FCSTD DOCUMENT  (FreeCAD 0.19R24291 (Git))
Label: v1-180-assembly
License: Other
LicenseURL: GPL3
objects: App::Link×50, App::Part×6, App::DocumentObjectGroup×2, PartDesign::CoordinateSystem×1, App::FeaturePython×1
note: 1 computed B-rep shape members (.brp) not serialized (recipe doc carries the construction recipe, not evaluated geometry)
EXTERNAL_REF file=../WIP/component-assembly/frame-assembly.FCStd obj=LCS_main_frame
EXTERNAL_REF file=../WIP/component-assembly/frame-assembly.FCStd obj=Part054
EXTERNAL_REF file=../WIP/component-assembly/foot-assembly.FCStd obj=LCS_foot
EXTERNAL_REF file=../WIP/component-assembly/foot-assembly.FCStd obj=Part
EXTERNAL_REF file=../WIP/component-assembly/ab-x-motor-assembly.FCStd obj=LCS_ab_x_motor
EXTERNAL_REF file=../WIP/component-assembly/ab-x-motor-assembly.FCStd obj=Part
EXTERNAL_REF file=../WIP/component-assembly/ab-y-motor-assembly.FCStd obj=LCS_ab_y_motor
EXTERNAL_REF file=../WIP/component-assembly/ab-y-motor-assembly.FCStd obj=Part
EXTERNAL_REF file=../WIP/component-assembly/linear-rail-assembly.FCStd obj=LCS_0001
EXTERNAL_REF file=../WIP/component-assembly/linear-rail-assembly.FCStd obj=y_rails
EXTERNAL_REF file=../WIP/component-assembly/linear-rail-assembly.FCStd obj=LCS_0002
EXTERNAL_REF file=../WIP/component-assembly/linear-rail-assembly.FCStd obj=z_rails
EXTERNAL_REF file=../WIP/component-assembly/y-carrier-left-1515-assembly.FCStd obj=LCS_Y_carrier_left
EXTERNAL_REF file=../WIP/component-assembly/y-carrier-left-1515-assembly.FCStd obj=Part
EXTERNAL_REF file=../WIP/component-assembly/y-carrier-right-1515-assembly.FCStd obj=LCS_Y_carrier_right
EXTERNAL_REF file=../WIP/component-assembly/y-carrier-right-1515-assembly.FCStd obj=Part
EXTERNAL_REF file=../WIP/component-assembly/linear-rail-assembly.FCStd obj=LCS_0
EXTERNAL_REF file=../WIP/component-assembly/linear-rail-assembly.FCStd obj=x_rail
EXTERNAL_REF file=../WIP/component-assembly/z-motor-left-assembly.FCStd obj=LCS_z_motor_left
EXTERNAL_REF file=../WIP/component-assembly/z-motor-left-assembly.FCStd obj=Part
EXTERNAL_REF file=../WIP/component-assembly/z-motor-right-assembly.FCStd obj=LCS_z_motor_right
EXTERNAL_REF file=../WIP/component-assembly/z-motor-right-assembly.FCStd obj=Part
EXTERNAL_REF file=../WIP/component-assembly/bed-assembly.FCStd obj=LCS_0
EXTERNAL_REF file=../WIP/component-assembly/bed-assembly.FCStd obj=bed_assembly
EXTERNAL_REF file=../WIP/component-assembly/z-belt-assembly.FCStd obj=LCS_z_belt
EXTERNAL_REF file=../WIP/component-assembly/z-belt-assembly.FCStd obj=Part
EXTERNAL_REF file=../WIP/component-assembly/xy-belt-assembly.FCStd obj=LCS_xy_belt
EXTERNAL_REF file=../WIP/component-assembly/xy-belt-assembly.FCStd obj=Part
EXTERNAL_REF file=../WIP/component-assembly/bottom-panel-assembly.FCStd obj=LCS_bottom_panel_assembly
EXTERNAL_REF file=../WIP/component-assembly/bottom-panel-assembly.FCStd obj=Part007
EXTERNAL_REF file=../WIP/component-assembly/extruder-cable-end-assembly.FCStd obj=LCS_extruder_cable_mounter
EXTERNAL_REF file=../WIP/component-assembly/extruder-cable-end-assembly.FCStd obj=Part198
EXTERNAL_REF file=../WIP/component-assembly/y-endstop-assembly.FCStd obj=LCS_y_endstop
EXTERNAL_REF file=../WIP/component-assembly/y-endstop-assembly.FCStd obj=Part
EXTERNAL_REF file=../WIP/component-assembly/x-endstop-flag-assembly.FCStd obj=LCS_x_endstop_flag
EXTERNAL_REF file=../WIP/component-assembly/x-endstop-flag-assembly.FCStd obj=Part001
EXTERNAL_REF file=../WIP/component-assembly/sherpa-mini-assembly.FCStd obj=LCS_sherpa_mini
EXTERNAL_REF file=../WIP/component-assembly/sherpa-mini-assembly.FCStd obj=Part
EXTERNAL_REF file=../WIP/component-assembly/z-block-mount-left-assembly.FCStd obj=LCS_z_rail_block_mount_y_slider_1
EXTERNAL_REF file=../WIP/component-assembly/z-block-mount-left-assembly.FCStd obj=Part
EXTERNAL_REF file=../WIP/component-assembly/z-idler-left-assembly.FCStd obj=LCS_Z_idler_left
EXTERNAL_REF file=../WIP/component-assembly/z-idler-left-assembly.FCStd obj=Part
EXTERNAL_REF file=../WIP/component-assembly/z-idler-right-assembly.FCStd obj=LCS_Z_idler_right
EXTERNAL_REF file=../WIP/component-assembly/z-idler-right-assembly.FCStd obj=Part001
EXTERNAL_REF file=../WIP/component-assembly/addon-filament-guide-arm-assembly.FCStd obj=LCS_filament_guide
EXTERNAL_REF file=../WIP/component-assembly/addon-filament-guide-arm-assembly.FCStd obj=Part002
EXTERNAL_REF file=../WIP/component-assembly/front-left-idler-assembly.FCStd obj=LCS_left_idler
EXTERNAL_REF file=../WIP/component-assembly/front-left-idler-assembly.FCStd obj=Part
EXTERNAL_REF file=../WIP/component-assembly/front-right-idler-assembly.FCStd obj=LCS_right_idler
EXTERNAL_REF file=../WIP/component-assembly/front-right-idler-assembly.FCStd obj=Part001
EXTERNAL_REF file=../WIP/component-assembly/addon-camera-assembly.FCStd obj=LCS_camera
EXTERNAL_REF file=../WIP/component-assembly/addon-camera-assembly.FCStd obj=Part001
EXTERNAL_REF file=../WIP/component-assembly/spool-holder-assembly.FCStd obj=LCS_spool_holder
EXTERNAL_REF file=../WIP/component-assembly/spool-holder-assembly.FCStd obj=Part196
EXTERNAL_REF file=../WIP/component-assembly/LCD-assembly.FCStd obj=LCS_LCD
EXTERNAL_REF file=../WIP/component-assembly/LCD-assembly.FCStd obj=Part
EXTERNAL_REF file=../WIP/component-assembly/left-panel-assembly.FCStd obj=LCS_left_panel
EXTERNAL_REF file=../WIP/component-assembly/left-panel-assembly.FCStd obj=Part025
EXTERNAL_REF file=../WIP/component-assembly/top-panel-assembly.FCStd obj=LCS_top_panel
EXTERNAL_REF file=../WIP/component-assembly/top-panel-assembly.FCStd obj=Part042
EXTERNAL_REF file=../WIP/component-assembly/rear-bottom-panel-assembly.FCStd obj=LCS_back_bottom_panel
EXTERNAL_REF file=../WIP/component-assembly/rear-bottom-panel-assembly.FCStd obj=Part003
EXTERNAL_REF file=../WIP/component-assembly/rear-top-panel-assembly.FCStd obj=LCS_back_top_panel
EXTERNAL_REF file=../WIP/component-assembly/rear-top-panel-assembly.FCStd obj=Part004
EXTERNAL_REF file=../WIP/component-assembly/front-panel-assembly.FCStd obj=LCS_front_panel
EXTERNAL_REF file=../WIP/component-assembly/front-panel-assembly.FCStd obj=Part046
EXTERNAL_REF file=../WIP/component-assembly/neo-pixel-assembly.FCStd obj=LCS_neopizel
EXTERNAL_REF file=../WIP/component-assembly/neo-pixel-assembly.FCStd obj=Part
EXTERNAL_REF file=../WIP/component-assembly/cherrymz-button-assembly.FCStd obj=LCS_cherrymx_button
EXTERNAL_REF file=../WIP/component-assembly/cherrymz-button-assembly.FCStd obj=Part
EXTERNAL_REF file=../WIP/component-assembly/air-filter-assembly.FCStd obj=LCS_air_filter
EXTERNAL_REF file=../WIP/component-assembly/air-filter-assembly.FCStd obj=Part
EXTERNAL_REF file=../WIP/component-assembly/add-on-ptfe-tube-guide-assembly.FCStd obj=LCS_ptfe_tube_guide
EXTERNAL_REF file=../WIP/component-assembly/add-on-ptfe-tube-guide-assembly.FCStd obj=Part
EXTERNAL_REF file=../WIP/component-assembly/counter-weight-spring-box-assembly.FCStd obj=LCS_counter_spring_box
EXTERNAL_REF file=../WIP/component-assembly/counter-weight-spring-box-assembly.FCStd obj=Part
EXTERNAL_REF file=../WIP/component-assembly/counter-weight-spring-box-assembly.FCStd obj=LCS_counter_weight_top_arm
EXTERNAL_REF file=../WIP/component-assembly/counter-weight-spring-box-assembly.FCStd obj=Part001
EXTERNAL_REF file=../WIP/component-assembly/z-block-mount-right-counter-weight-assembly.FCStd obj=LCS_z_rail_block_mount_x_slider
EXTERNAL_REF file=../WIP/component-assembly/z-block-mount-right-counter-weight-assembly.FCStd obj=Part001
EXTERNAL_REF file=../WIP/component-assembly/toolhead-sherpa-pcb-1515-assembly.FCStd obj=LCS_toolhead_1515
EXTERNAL_REF file=../WIP/component-assembly/toolhead-sherpa-pcb-1515-assembly.FCStd obj=Part197
EXTERNAL_REF file=../WIP/component-assembly/right-panel-assembly.FCStd obj=LCS_right_panel
EXTERNAL_REF file=../WIP/component-assembly/right-panel-assembly.FCStd obj=Part005
EXTERNAL_REF file=../WIP/component-assembly/side-blower-4028-assembly.FCStd obj=LCS_aux_fan
EXTERNAL_REF file=../WIP/component-assembly/side-blower-4028-assembly.FCStd obj=Part

FEATURE [App::DocumentObjectGroup] Parts
FEATURE [PartDesign::CoordinateSystem] LCS_Origin
  AttacherType = Attacher::AttachEngine3D
  MapMode = 2
  Support = -> [X_Axis]
FEATURE [App::DocumentObjectGroup] Constraints
FEATURE [App::FeaturePython] Variables  # WARN: FeaturePython — macro-defined, semantics opaque (R4)
FEATURE [App::Link] frame_assembly_main_frame  label="frame"
  AssemblyType = Asm4EE
  AttachedBy = #LCS_main_frame
  AttachedTo = Parent Assembly#LCS_Origin
  ElementCount = 0
  LinkTransform = false
  Scale = 1
  ScaleVector = (1,1,1)
  ShowElement = true
  expr: Placement = LCS_Origin.Placement * AttachmentOffset * frame_assembly#LCS_main_frame.Placement ^ -1
FEATURE [App::Link] Unnamed2_foot  label="foot-1"
  AssemblyType = Asm4EE
  AttachedBy = #LCS_foot
  AttachedTo = Parent Assembly#LCS_Origin
  AttachmentOffset = pos=(-170,15,-30) rot=(0,0,1;3.14159rad)
  ElementCount = 0
  LinkPlacement = pos=(-170,15,-30) rot=(0,0,1;3.14159rad)
  LinkTransform = false
  Placement = pos=(-170,15,-30) rot=(0,0,1;3.14159rad)
  Scale = 1
  ScaleVector = (1,1,1)
  ShowElement = true
  expr: Placement = LCS_Origin.Placement * AttachmentOffset * foot_assembly#LCS_foot.Placement ^ -1
FEATURE [App::Link] Unnamed2_foot001  label="foot-2"
  AssemblyType = Asm4EE
  AttachedBy = #LCS_foot
  AttachedTo = Parent Assembly#LCS_Origin
  AttachmentOffset = pos=(170,15,-30) rot=(0,0,1;4.71239rad)
  ElementCount = 0
  LinkPlacement = pos=(170,15,-30) rot=(0,0,1;4.71239rad)
  LinkTransform = false
  Placement = pos=(170,15,-30) rot=(0,0,1;4.71239rad)
  Scale = 1
  ScaleVector = (1,1,1)
  ShowElement = true
  expr: Placement = LCS_Origin.Placement * AttachmentOffset * foot_assembly#LCS_foot.Placement ^ -1
FEATURE [App::Link] Unnamed2_foot002  label="foot-3"
  AssemblyType = Asm4EE
  AttachedBy = #LCS_foot
  AttachedTo = Parent Assembly#LCS_Origin
  AttachmentOffset = pos=(170,355,-30) rot=(0,0,1;0rad)
  ElementCount = 0
  LinkPlacement = pos=(170,355,-30) rot=(0,0,1;0rad)
  LinkTransform = false
  Placement = pos=(170,355,-30) rot=(0,0,1;0rad)
  Scale = 1
  ScaleVector = (1,1,1)
  ShowElement = true
  expr: Placement = LCS_Origin.Placement * AttachmentOffset * foot_assembly#LCS_foot.Placement ^ -1
FEATURE [App::Link] Unnamed2_foot003  label="foot-4"
  AssemblyType = Asm4EE
  AttachedBy = #LCS_foot
  AttachedTo = Parent Assembly#LCS_Origin
  AttachmentOffset = pos=(-170,355,-30) rot=(0,0,1;1.5708rad)
  ElementCount = 0
  LinkPlacement = pos=(-170,355,-30) rot=(0,0,1;1.5708rad)
  LinkTransform = false
  Placement = pos=(-170,355,-30) rot=(0,0,1;1.5708rad)
  Scale = 1
  ScaleVector = (1,1,1)
  ShowElement = true
  expr: Placement = LCS_Origin.Placement * AttachmentOffset * foot_assembly#LCS_foot.Placement ^ -1
FEATURE [App::Link] left_motor_assembly_ab_x_motor  label="ab-x-motor"
  AssemblyType = Asm4EE
  AttachedBy = #LCS_ab_x_motor
  AttachedTo = Parent Assembly#LCS_Origin
  AttachmentOffset = pos=(-155,370,310) rot=(0,0,1;0rad)
  ElementCount = 0
  LinkPlacement = pos=(-155,370,310) rot=(0,0,1;0rad)
  LinkTransform = false
  Placement = pos=(-155,370,310) rot=(0,0,1;0rad)
  Scale = 1
  ScaleVector = (1,1,1)
  ShowElement = true
  expr: Placement = LCS_Origin.Placement * AttachmentOffset * ab_x_motor_assembly#LCS_ab_x_motor.Placement ^ -1
FEATURE [App::Link] right_motor_assembly_ab_y_motor  label="ab-y-motor"
  AssemblyType = Asm4EE
  AttachedBy = #LCS_ab_y_motor
  AttachedTo = Parent Assembly#LCS_Origin
  AttachmentOffset = pos=(155,370,310) rot=(0,0,1;0rad)
  ElementCount = 0
  LinkPlacement = pos=(155,370,310) rot=(0,0,1;0rad)
  LinkTransform = false
  Placement = pos=(155,370,310) rot=(0,0,1;0rad)
  Scale = 1
  ScaleVector = (1,1,1)
  ShowElement = true
  expr: Placement = LCS_Origin.Placement * AttachmentOffset * ab_y_motor_assembly#LCS_ab_y_motor.Placement ^ -1
FEATURE [App::Link] linear_rail_assembly_y_rails  label="y_rails"
  AssemblyType = Asm4EE
  AttachedBy = #LCS_0001
  AttachedTo = Parent Assembly#LCS_Origin
  ElementCount = 0
  LinkTransform = false
  Scale = 1
  ScaleVector = (1,1,1)
  ShowElement = true
  expr: Placement = LCS_Origin.Placement * AttachmentOffset * linear_rail_assembly#LCS_0001.Placement ^ -1
FEATURE [App::Link] linear_rail_assembly_z_rails  label="z_rails"
  AssemblyType = Asm4EE
  AttachedBy = #LCS_0002
  AttachedTo = Parent Assembly#LCS_Origin
  ElementCount = 0
  LinkTransform = false
  Scale = 1
  ScaleVector = (1,1,1)
  ShowElement = true
  expr: Placement = LCS_Origin.Placement * AttachmentOffset * linear_rail_assembly#LCS_0002.Placement ^ -1
FEATURE [App::Link] Y_carrier_left  label="Y-carrier-left"
  AssemblyType = Asm4EE
  AttachedBy = #LCS_Y_carrier_left
  AttachedTo = Parent Assembly#LCS_Origin
  AttachmentOffset = pos=(-156,203,310) rot=(0,0,1;0rad)
  ElementCount = 0
  LinkPlacement = pos=(-156,203,310) rot=(0,0,1;0rad)
  LinkTransform = false
  Placement = pos=(-156,203,310) rot=(0,0,1;0rad)
  Scale = 1
  ScaleVector = (1,1,1)
  ShowElement = true
  expr: Placement = LCS_Origin.Placement * AttachmentOffset * y_carrier_left_1515_assembly#LCS_Y_carrier_left.Placement ^ -1
FEATURE [App::Link] Y_carrier_right  label="Y-carrier-right"
  AssemblyType = Asm4EE
  AttachedBy = #LCS_Y_carrier_right
  AttachedTo = Parent Assembly#LCS_Origin
  AttachmentOffset = pos=(155,203,310) rot=(0,0,1;0rad)
  ElementCount = 0
  LinkPlacement = pos=(155,203,310) rot=(0,0,1;0rad)
  LinkTransform = false
  Placement = pos=(155,203,310) rot=(0,0,1;0rad)
  Scale = 1
  ScaleVector = (1,1,1)
  ShowElement = true
  expr: Placement = LCS_Origin.Placement * AttachmentOffset * y_carrier_right_1515_assembly#LCS_Y_carrier_right.Placement ^ -1
FEATURE [App::Link] linear_rail_assembly_x_rail  label="x_rail"
  AssemblyType = Asm4EE
  AttachedBy = #LCS_0
  AttachedTo = Parent Assembly#LCS_Origin
  AttachmentOffset = pos=(0,0,-2.5) rot=(0,0,1;0rad)
  ElementCount = 0
  LinkPlacement = pos=(0,0,-2.5) rot=(0,0,1;0rad)
  LinkTransform = false
  Placement = pos=(0,0,-2.5) rot=(0,0,1;0rad)
  Scale = 1
  ScaleVector = (1,1,1)
  ShowElement = true
  expr: Placement = LCS_Origin.Placement * AttachmentOffset * linear_rail_assembly#LCS_0.Placement ^ -1
FEATURE [App::Link] z_motor_left_assembly_z_motor_left  label="z-motor-left-front"
  AssemblyType = Asm4EE
  AttachedBy = #LCS_z_motor_left
  AttachedTo = Parent Assembly#LCS_Origin
  AttachmentOffset = pos=(-155,117,0) rot=(0,0,1;0rad)
  ElementCount = 0
  LinkPlacement = pos=(-155,117,0) rot=(0,0,1;0rad)
  LinkTransform = false
  Placement = pos=(-155,117,0) rot=(0,0,1;0rad)
  Scale = 1
  ScaleVector = (1,1,1)
  ShowElement = true
  expr: Placement = LCS_Origin.Placement * AttachmentOffset * z_motor_left_assembly#LCS_z_motor_left.Placement ^ -1
FEATURE [App::Link] z_motor_left_back  label="z-motor-left-back"
  AssemblyType = Asm4EE
  AttachedBy = #LCS_z_motor_left
  AttachedTo = Parent Assembly#LCS_Origin
  AttachmentOffset = pos=(-155,287,0) rot=(0,0,1;0rad)
  ElementCount = 0
  LinkPlacement = pos=(-155,287,0) rot=(0,0,1;0rad)
  LinkTransform = false
  Placement = pos=(-155,287,0) rot=(0,0,1;0rad)
  Scale = 1
  ScaleVector = (1,1,1)
  ShowElement = true
  expr: Placement = LCS_Origin.Placement * AttachmentOffset * z_motor_left_assembly#LCS_z_motor_left.Placement ^ -1
FEATURE [App::Link] z_motor_right  label="z-motor-right"
  AssemblyType = Asm4EE
  AttachedBy = #LCS_z_motor_right
  AttachedTo = Parent Assembly#LCS_Origin
  AttachmentOffset = pos=(155,202,0) rot=(0,0,1;3.14159rad)
  ElementCount = 0
  LinkPlacement = pos=(155,202,0) rot=(0,0,1;3.14159rad)
  LinkTransform = false
  Placement = pos=(155,202,0) rot=(0,0,1;3.14159rad)
  Scale = 1
  ScaleVector = (1,1,1)
  ShowElement = true
  expr: Placement = LCS_Origin.Placement * AttachmentOffset * z_motor_right_assembly#LCS_z_motor_right.Placement ^ -1
FEATURE [App::Link] bed_1515_180mm  label="bed_1515-180mm"
  AssemblyType = Asm4EE
  AttachedBy = #LCS_0
  AttachedTo = Parent Assembly#LCS_Origin
  AttachmentOffset = pos=(0,130,140) rot=(0,0,1;0rad)
  ElementCount = 0
  LinkPlacement = pos=(0,130,140) rot=(0,0,1;0rad)
  LinkTransform = false
  Placement = pos=(0,130,140) rot=(0,0,1;0rad)
  Scale = 1
  ScaleVector = (1,1,1)
  ShowElement = true
  expr: Placement = LCS_Origin.Placement * AttachmentOffset * bed_assembly#LCS_0.Placement ^ -1
FEATURE [App::Link] z_belts  label="z-belts"
  AssemblyType = Asm4EE
  AttachedBy = #LCS_z_belt
  AttachedTo = Parent Assembly#LCS_Origin
  ElementCount = 0
  LinkTransform = false
  Scale = 1
  ScaleVector = (1,1,1)
  ShowElement = true
  expr: Placement = LCS_Origin.Placement * AttachmentOffset * z_belt_assembly#LCS_z_belt.Placement ^ -1
FEATURE [App::Link] xy_belt  label="xy-belt"
  AssemblyType = Asm4EE
  AttachedBy = #LCS_xy_belt
  AttachedTo = Parent Assembly#LCS_Origin
  ElementCount = 0
  LinkTransform = false
  Scale = 1
  ScaleVector = (1,1,1)
  ShowElement = true
  expr: Placement = LCS_Origin.Placement * AttachmentOffset * xy_belt_assembly#LCS_xy_belt.Placement ^ -1
FEATURE [App::Link] bottom_panel_assembly  label="bottom-panel"
  AssemblyType = Asm4EE
  AttachedBy = #LCS_bottom_panel_assembly
  AttachedTo = Parent Assembly#LCS_Origin
  AttachmentOffset = pos=(0,185,0) rot=(0,0,1;0rad)
  ElementCount = 0
  LinkPlacement = pos=(0,185,0) rot=(0,0,1;0rad)
  LinkTransform = false
  Placement = pos=(0,185,0) rot=(0,0,1;0rad)
  Scale = 1
  ScaleVector = (1,1,1)
  ShowElement = true
  expr: Placement = LCS_Origin.Placement * AttachmentOffset * bottom_panel_assembly#LCS_bottom_panel_assembly.Placement ^ -1
FEATURE [App::Link] extruder_cable_mounter  label="extruder-cable-mounter"
  AssemblyType = Asm4EE
  AttachedBy = #LCS_extruder_cable_mounter
  AttachedTo = Parent Assembly#LCS_Origin
  AttachmentOffset = pos=(127,330,472) rot=(0,0,1;0rad)
  ElementCount = 0
  LinkPlacement = pos=(127,330,472) rot=(0,0,1;0rad)
  LinkTransform = false
  Placement = pos=(127,330,472) rot=(0,0,1;0rad)
  Scale = 1
  ScaleVector = (1,1,1)
  ShowElement = true
  expr: Placement = LCS_Origin.Placement * AttachmentOffset * extruder_cable_end_assembly#LCS_extruder_cable_mounter.Placement ^ -1
FEATURE [App::Link] y_endstop  label="y-endstop"
  AttachedBy = #LCS_y_endstop
  AttachedTo = Parent Assembly#LCS_Origin
  AttachmentOffset = pos=(-170,296,345) rot=(0,0,1;0rad)
  ElementCount = 0
  LinkPlacement = pos=(-170,296,345) rot=(0,0,1;0rad)
  LinkTransform = false
  Placement = pos=(-170,296,345) rot=(0,0,1;0rad)
  Scale = 1
  ScaleVector = (1,1,1)
  ShowElement = true
  SolverId = Placement::ExpressionEngine
  expr: Placement = LCS_Origin.Placement * AttachmentOffset * y_endstop_assembly#LCS_y_endstop.Placement ^ -1
FEATURE [App::Link] x_endstop_flag001  label="x-endstop-flag"
  AttachedBy = #LCS_x_endstop_flag
  AttachedTo = Parent Assembly#LCS_Origin
  AttachmentOffset = pos=(131,203,363) rot=(0,0,1;0rad)
  ElementCount = 0
  LinkPlacement = pos=(131,203,363) rot=(0,0,1;0rad)
  LinkTransform = false
  Placement = pos=(131,203,363) rot=(0,0,1;0rad)
  Scale = 1
  ScaleVector = (1,1,1)
  ShowElement = true
  SolverId = Placement::ExpressionEngine
  expr: Placement = LCS_Origin.Placement * AttachmentOffset * x_endstop_flag_assembly#LCS_x_endstop_flag.Placement ^ -1
FEATURE [App::Link] sherpa_mini  label="sherpa-mini"
  AttachedBy = #LCS_sherpa_mini
  AttachedTo = Parent Assembly#LCS_Origin
  AttachmentOffset = pos=(0,204.5,313) rot=(0,0,1;0rad)
  ElementCount = 0
  LinkPlacement = pos=(0,204.5,313) rot=(0,0,1;0rad)
  LinkTransform = false
  Placement = pos=(0,204.5,313) rot=(0,0,1;0rad)
  Scale = 1
  ScaleVector = (1,1,1)
  ShowElement = true
  SolverId = Placement::ExpressionEngine
  expr: Placement = LCS_Origin.Placement * AttachmentOffset * sherpa_mini_assembly#LCS_sherpa_mini.Placement ^ -1
FEATURE [App::Link] z_rail_block_mount_left_front  label="z-rail-block-mount-left-front"
  AttachedBy = #LCS_z_rail_block_mount_y_slider_1
  AttachedTo = Parent Assembly#LCS_Origin
  AttachmentOffset = pos=(-142,45,102) rot=(0,0,1;0rad)
  ElementCount = 0
  LinkPlacement = pos=(-142,45,102) rot=(0,0,1;0rad)
  LinkTransform = false
  Placement = pos=(-142,45,102) rot=(0,0,1;0rad)
  Scale = 1
  ScaleVector = (1,1,1)
  ShowElement = true
  SolverId = Placement::ExpressionEngine
  expr: Placement = LCS_Origin.Placement * AttachmentOffset * z_block_mount_left_assembly#LCS_z_rail_block_mount_y_slider_1.Placement ^ -1
FEATURE [App::Link] z_rail_block_mount_left_back  label="z-rail-block-mount-left-back"
  AttachedBy = #LCS_z_rail_block_mount_y_slider_1
  AttachedTo = Parent Assembly#LCS_Origin
  AttachmentOffset = pos=(-142,215,102) rot=(0,0,1;0rad)
  ElementCount = 0
  LinkPlacement = pos=(-142,215,102) rot=(0,0,1;0rad)
  LinkTransform = false
  Placement = pos=(-142,215,102) rot=(0,0,1;0rad)
  Scale = 1
  ScaleVector = (1,1,1)
  ShowElement = true
  SolverId = Placement::ExpressionEngine
  expr: Placement = LCS_Origin.Placement * AttachmentOffset * z_block_mount_left_assembly#LCS_z_rail_block_mount_y_slider_1.Placement ^ -1
FEATURE [App::Link] Z_idler_left_front  label="Z-idler-left-front"
  AttachedBy = #LCS_Z_idler_left
  AttachedTo = Parent Assembly#LCS_Origin
  AttachmentOffset = pos=(-155,76,282) rot=(0,0,1;0rad)
  ElementCount = 0
  LinkPlacement = pos=(-155,76,282) rot=(0,0,1;0rad)
  LinkTransform = false
  Placement = pos=(-155,76,282) rot=(0,0,1;0rad)
  Scale = 1
  ScaleVector = (1,1,1)
  ShowElement = true
  SolverId = Placement::ExpressionEngine
  expr: Placement = LCS_Origin.Placement * AttachmentOffset * z_idler_left_assembly#LCS_Z_idler_left.Placement ^ -1
FEATURE [App::Link] Z_idler_left_back  label="Z-idler-left-back"
  AttachedBy = #LCS_Z_idler_left
  AttachedTo = Parent Assembly#LCS_Origin
  AttachmentOffset = pos=(-155,246,282) rot=(0,0,1;0rad)
  ElementCount = 0
  LinkPlacement = pos=(-155,246,282) rot=(0,0,1;0rad)
  LinkTransform = false
  Placement = pos=(-155,246,282) rot=(0,0,1;0rad)
  Scale = 1
  ScaleVector = (1,1,1)
  ShowElement = true
  SolverId = Placement::ExpressionEngine
  expr: Placement = LCS_Origin.Placement * AttachmentOffset * z_idler_left_assembly#LCS_Z_idler_left.Placement ^ -1
FEATURE [App::Link] Z_idler_right_middle  label="Z-idler-right-middle"
  AttachedBy = #LCS_Z_idler_right
  AttachedTo = Parent Assembly#LCS_Origin
  AttachmentOffset = pos=(155,161,282) rot=(0,0,1;0rad)
  ElementCount = 0
  LinkPlacement = pos=(155,161,282) rot=(0,0,1;0rad)
  LinkTransform = false
  Placement = pos=(155,161,282) rot=(0,0,1;0rad)
  Scale = 1
  ScaleVector = (1,1,1)
  ShowElement = true
  SolverId = Placement::ExpressionEngine
  expr: Placement = LCS_Origin.Placement * AttachmentOffset * z_idler_right_assembly#LCS_Z_idler_right.Placement ^ -1
FEATURE [App::Link] filament_guide  label="filament-guide"
  AttachedBy = #LCS_filament_guide
  AttachedTo = Parent Assembly#LCS_Origin
  AttachmentOffset = pos=(170,341,215) rot=(0,0,1;0rad)
  ElementCount = 0
  LinkPlacement = pos=(170,341,215) rot=(0,0,1;0rad)
  LinkTransform = false
  Placement = pos=(170,341,215) rot=(0,0,1;0rad)
  Scale = 1
  ScaleVector = (1,1,1)
  ShowElement = true
  SolverId = Placement::ExpressionEngine
  expr: Placement = LCS_Origin.Placement * AttachmentOffset * addon_filament_guide_arm_assembly#LCS_filament_guide.Placement ^ -1
FEATURE [App::Link] front_left_idler  label="front-left-idler"
  AttachedBy = #LCS_left_idler
  AttachedTo = Parent Assembly#LCS_Origin
  AttachmentOffset = pos=(-155,0,310) rot=(0,0,1;0rad)
  ElementCount = 0
  LinkPlacement = pos=(-155,0,310) rot=(0,0,1;0rad)
  LinkTransform = false
  Placement = pos=(-155,0,310) rot=(0,0,1;0rad)
  Scale = 1
  ScaleVector = (1,1,1)
  ShowElement = true
  SolverId = Placement::ExpressionEngine
  expr: Placement = LCS_Origin.Placement * AttachmentOffset * front_left_idler_assembly#LCS_left_idler.Placement ^ -1
FEATURE [App::Link] front_right_idler  label="front-right-idler"
  AttachedBy = #LCS_right_idler
  AttachedTo = Parent Assembly#LCS_Origin
  AttachmentOffset = pos=(155,0,310) rot=(0,0,1;0rad)
  ElementCount = 0
  LinkPlacement = pos=(155,0,310) rot=(0,0,1;0rad)
  LinkTransform = false
  Placement = pos=(155,0,310) rot=(0,0,1;0rad)
  Scale = 1
  ScaleVector = (1,1,1)
  ShowElement = true
  SolverId = Placement::ExpressionEngine
  expr: Placement = LCS_Origin.Placement * AttachmentOffset * front_right_idler_assembly#LCS_right_idler.Placement ^ -1
FEATURE [App::Link] camera
  AttachedBy = #LCS_camera
  AttachedTo = Parent Assembly#LCS_Origin
  AttachmentOffset = pos=(-142,313,300) rot=(0,0,1;0rad)
  ElementCount = 0
  LinkPlacement = pos=(-142,313,300) rot=(0,0,1;0rad)
  LinkTransform = false
  Placement = pos=(-142,313,300) rot=(0,0,1;0rad)
  Scale = 1
  ScaleVector = (1,1,1)
  ShowElement = true
  SolverId = Placement::ExpressionEngine
  expr: Placement = LCS_Origin.Placement * AttachmentOffset * addon_camera_assembly#LCS_camera.Placement ^ -1
FEATURE [App::Link] spool_holder  label="spool-holder"
  AttachedBy = #LCS_spool_holder
  AttachedTo = Parent Assembly#LCS_Origin
  AttachmentOffset = pos=(0,289,30) rot=(0,0,1;0rad)
  ElementCount = 0
  LinkPlacement = pos=(0,289,30) rot=(0,0,1;0rad)
  LinkTransform = false
  Placement = pos=(0,289,30) rot=(0,0,1;0rad)
  Scale = 1
  ScaleVector = (1,1,1)
  ShowElement = true
  SolverId = Placement::ExpressionEngine
  expr: Placement = LCS_Origin.Placement * AttachmentOffset * spool_holder_assembly#LCS_spool_holder.Placement ^ -1
FEATURE [App::Link] LCD_retro  label="LCD-retro"
  AttachedBy = #LCS_LCD
  AttachedTo = Parent Assembly#LCS_Origin
  AttachmentOffset = pos=(0,160,-14) rot=(0,0,1;0rad)
  ElementCount = 0
  LinkPlacement = pos=(0,160,-14) rot=(0,0,1;0rad)
  LinkTransform = false
  Placement = pos=(0,160,-14) rot=(0,0,1;0rad)
  Scale = 1
  ScaleVector = (1,1,1)
  ShowElement = true
  SolverId = Placement::ExpressionEngine
  expr: Placement = LCS_Origin.Placement * AttachmentOffset * LCD_assembly#LCS_LCD.Placement ^ -1
FEATURE [App::Link] left_panel  label="left-panel"
  AttachedBy = #LCS_left_panel
  AttachedTo = Parent Assembly#LCS_Origin
  AttachmentOffset = pos=(-188,25,475) rot=(-0.707107,-0.707107,0;3.14159rad)
  ElementCount = 0
  LinkPlacement = pos=(-188,25,475) rot=(-0.707107,-0.707107,0;3.14159rad)
  LinkTransform = false
  Placement = pos=(-188,25,475) rot=(-0.707107,-0.707107,0;3.14159rad)
  Scale = 1
  ScaleVector = (1,1,1)
  ShowElement = true
  SolverId = Placement::ExpressionEngine
  expr: Placement = LCS_Origin.Placement * AttachmentOffset * left_panel_assembly#LCS_left_panel.Placement ^ -1
FEATURE [App::Link] top_panel  label="top-panel"
  AttachedBy = #LCS_top_panel
  AttachedTo = Parent Assembly#LCS_Origin
  AttachmentOffset = pos=(0,185,500) rot=(0,0,1;0rad)
  ElementCount = 0
  LinkPlacement = pos=(0,185,500) rot=(0,0,1;0rad)
  LinkTransform = false
  Placement = pos=(0,185,500) rot=(0,0,1;0rad)
  Scale = 1
  ScaleVector = (1,1,1)
  ShowElement = true
  SolverId = Placement::ExpressionEngine
  expr: Placement = LCS_Origin.Placement * AttachmentOffset * top_panel_assembly#LCS_top_panel.Placement ^ -1
FEATURE [App::Part] Part  label="foot"
  Group = -> [Unnamed2_foot,Unnamed2_foot001,Unnamed2_foot002,Unnamed2_foot003,top_panel]
  Origin = -> Origin001
FEATURE [App::Link] rear_bottom_panel  label="rear-bottom-panel"
  AttachedBy = #LCS_back_bottom_panel
  AttachedTo = Parent Assembly#LCS_Origin
  AttachmentOffset = pos=(0,340,141) rot=(0,-0.707107,0.707107;3.14159rad)
  ElementCount = 0
  LinkPlacement = pos=(0,340,141) rot=(0,-0.707107,0.707107;3.14159rad)
  LinkTransform = false
  Placement = pos=(0,340,141) rot=(0,-0.707107,0.707107;3.14159rad)
  Scale = 1
  ScaleVector = (1,1,1)
  ShowElement = true
  SolverId = Placement::ExpressionEngine
  expr: Placement = LCS_Origin.Placement * AttachmentOffset * rear_bottom_panel_assembly#LCS_back_bottom_panel.Placement ^ -1
FEATURE [App::Link] rear_top_panel  label="rear-top-panel"
  AttachedBy = #LCS_back_top_panel
  AttachedTo = Parent Assembly#LCS_Origin
  AttachmentOffset = pos=(0,370,362.5) rot=(0,0.707107,0.707107;3.14159rad)
  ElementCount = 0
  LinkPlacement = pos=(0,370,362.5) rot=(0,0.707107,0.707107;3.14159rad)
  LinkTransform = false
  Placement = pos=(0,370,362.5) rot=(0,0.707107,0.707107;3.14159rad)
  Scale = 1
  ScaleVector = (1,1,1)
  ShowElement = true
  SolverId = Placement::ExpressionEngine
  expr: Placement = LCS_Origin.Placement * AttachmentOffset * rear_top_panel_assembly#LCS_back_top_panel.Placement ^ -1
FEATURE [App::Link] front_panel  label="front-panel"
  AttachedBy = #LCS_front_panel
  AttachedTo = Parent Assembly#LCS_Origin
  AttachmentOffset = pos=(-185,30,23) rot=(0,0,1;0rad)
  ElementCount = 0
  LinkPlacement = pos=(-185,30,23) rot=(0,0,1;0rad)
  LinkTransform = false
  Placement = pos=(-185,30,23) rot=(0,0,1;0rad)
  Scale = 1
  ScaleVector = (1,1,1)
  ShowElement = true
  SolverId = Placement::ExpressionEngine
  expr: Placement = LCS_Origin.Placement * AttachmentOffset * front_panel_assembly#LCS_front_panel.Placement ^ -1
FEATURE [App::Link] neo_pixel_mount_left  label="neo-pixel-mount-left"
  AttachedBy = #LCS_neopizel
  AttachedTo = Parent Assembly#LCS_Origin
  AttachmentOffset = pos=(-155,106,485) rot=(1,0,0;1.5708rad)
  ElementCount = 0
  LinkPlacement = pos=(-155,106,485) rot=(1,0,0;1.5708rad)
  LinkTransform = false
  Placement = pos=(-155,106,485) rot=(1,0,0;1.5708rad)
  Scale = 1
  ScaleVector = (1,1,1)
  ShowElement = true
  SolverId = Placement::ExpressionEngine
  expr: Placement = LCS_Origin.Placement * AttachmentOffset * neo_pixel_assembly#LCS_neopizel.Placement ^ -1
FEATURE [App::Link] neo_pixel_mount_right  label="neo-pixel-mount-right"
  AttachedBy = #LCS_neopizel
  AttachedTo = Parent Assembly#LCS_Origin
  AttachmentOffset = pos=(154,210,485) rot=(0,0.707107,0.707107;3.14159rad)
  ElementCount = 0
  LinkPlacement = pos=(154,210,485) rot=(0,0.707107,0.707107;3.14159rad)
  LinkTransform = false
  Placement = pos=(154,210,485) rot=(0,0.707107,0.707107;3.14159rad)
  Scale = 1
  ScaleVector = (1,1,1)
  ShowElement = true
  SolverId = Placement::ExpressionEngine
  expr: Placement = LCS_Origin.Placement * AttachmentOffset * neo_pixel_assembly#LCS_neopizel.Placement ^ -1
FEATURE [App::Link] cherrymx_button  label="cherrymx-button"
  AttachedBy = #LCS_cherrymx_button
  AttachedTo = Parent Assembly#LCS_Origin
  AttachmentOffset = pos=(-154,0,-26) rot=(0,0,1;0rad)
  ElementCount = 0
  LinkPlacement = pos=(-154,0,-26) rot=(0,0,1;0rad)
  LinkTransform = false
  Placement = pos=(-154,0,-26) rot=(0,0,1;0rad)
  Scale = 1
  ScaleVector = (1,1,1)
  ShowElement = true
  SolverId = Placement::ExpressionEngine
  expr: Placement = LCS_Origin.Placement * AttachmentOffset * cherrymz_button_assembly#LCS_cherrymx_button.Placement ^ -1
FEATURE [App::Link] air_filter  label="air-filter"
  AttachedBy = #LCS_air_filter
  AttachedTo = Parent Assembly#LCS_Origin
  AttachmentOffset = pos=(0,369,444) rot=(1,0,0;1.5708rad)
  ElementCount = 0
  LinkPlacement = pos=(0,369,444) rot=(1,0,0;1.5708rad)
  LinkTransform = false
  Placement = pos=(0,369,444) rot=(1,0,0;1.5708rad)
  Scale = 1
  ScaleVector = (1,1,1)
  ShowElement = true
  SolverId = Placement::ExpressionEngine
  expr: Placement = LCS_Origin.Placement * AttachmentOffset * air_filter_assembly#LCS_air_filter.Placement ^ -1
FEATURE [App::Link] ptfe_tube_guide  label="ptfe-tube-guide"
  AttachedBy = #LCS_ptfe_tube_guide
  AttachedTo = Parent Assembly#LCS_Origin
  AttachmentOffset = pos=(143,313,305) rot=(0.707107,0.707107,0;3.14159rad)
  ElementCount = 0
  LinkPlacement = pos=(143,313,305) rot=(0.707107,0.707107,0;3.14159rad)
  LinkTransform = false
  Placement = pos=(143,313,305) rot=(0.707107,0.707107,0;3.14159rad)
  Scale = 1
  ScaleVector = (1,1,1)
  ShowElement = true
  SolverId = Placement::ExpressionEngine
  expr: Placement = LCS_Origin.Placement * AttachmentOffset * add_on_ptfe_tube_guide_assembly#LCS_ptfe_tube_guide.Placement ^ -1
FEATURE [App::Part] Part004  label="add-on"
  Group = -> [filament_guide,spool_holder,camera,LCD_retro,neo_pixel_mount_right,neo_pixel_mount_left,cherrymx_button,air_filter,ptfe_tube_guide]
  Origin = -> Origin005
FEATURE [App::Link] counter_weight_sprintg_box  label="counter-weight-sprintg-box"
  AttachedBy = #LCS_counter_spring_box
  AttachedTo = Parent Assembly#LCS_Origin
  AttachmentOffset = pos=(155,64,89) rot=(0.707107,0,0.707107;3.14159rad)
  ElementCount = 0
  LinkPlacement = pos=(155,64,89) rot=(0.707107,0,0.707107;3.14159rad)
  LinkTransform = false
  Placement = pos=(155,64,89) rot=(0.707107,0,0.707107;3.14159rad)
  Scale = 1
  ScaleVector = (1,1,1)
  ShowElement = true
  SolverId = Placement::ExpressionEngine
  expr: Placement = LCS_Origin.Placement * AttachmentOffset * counter_weight_spring_box_assembly#LCS_counter_spring_box.Placement ^ -1
FEATURE [App::Link] counter_weight_top_arm  label="counter-weight-top-arm"
  AttachedBy = #LCS_counter_weight_top_arm
  AttachedTo = Parent Assembly#LCS_Origin
  AttachmentOffset = pos=(155,105,214) rot=(0.57735,0.57735,-0.57735;4.18879rad)
  ElementCount = 0
  LinkPlacement = pos=(155,105,214) rot=(0.57735,0.57735,-0.57735;4.18879rad)
  LinkTransform = false
  Placement = pos=(155,105,214) rot=(0.57735,0.57735,-0.57735;4.18879rad)
  Scale = 1
  ScaleVector = (1,1,1)
  ShowElement = true
  SolverId = Placement::ExpressionEngine
  expr: Placement = LCS_Origin.Placement * AttachmentOffset * counter_weight_spring_box_assembly#LCS_counter_weight_top_arm.Placement ^ -1
FEATURE [App::Link] z_rail_block_mount_x_slider_counter_weight  label="z-rail-block-mount-right-middle"
  AttachedBy = #LCS_z_rail_block_mount_x_slider
  AttachedTo = Parent Assembly#LCS_Origin
  AttachmentOffset = pos=(142,130,102) rot=(0,0,1;0rad)
  ElementCount = 0
  LinkPlacement = pos=(142,130,102) rot=(0,0,1;0rad)
  LinkTransform = false
  Placement = pos=(142,130,102) rot=(0,0,1;0rad)
  Scale = 1
  ScaleVector = (1,1,1)
  ShowElement = true
  SolverId = Placement::ExpressionEngine
  expr: Placement = LCS_Origin.Placement * AttachmentOffset * z_block_mount_right_counter_weight_assembly#LCS_z_rail_block_mount_x_slider.Placement ^ -1
FEATURE [App::Part] Part003  label="Z-axis"
  Group = -> [linear_rail_assembly_z_rails,z_motor_left_back,z_motor_right,z_motor_left_assembly_z_motor_left,bed_1515_180mm,z_belts,z_rail_block_mount_left_front,z_rail_block_mount_left_back,Z_idler_left_front,Z_idler_left_back,Z_idler_right_middle,counter_weight_sprintg_box,counter_weight_top_arm,z_rail_block_mount_x_slider_counter_weight]
  Origin = -> Origin004
FEATURE [App::Link] toolhead_sherp_pcb_1515  label="toolhead-sherp-pcb-1515"
  AttachedBy = #LCS_toolhead_1515
  AttachedTo = Parent Assembly#LCS_Origin
  AttachmentOffset = pos=(0,203,320) rot=(0,0,1;0rad)
  ElementCount = 0
  LinkPlacement = pos=(0,203,320) rot=(0,0,1;0rad)
  LinkTransform = false
  Placement = pos=(0,203,320) rot=(0,0,1;0rad)
  Scale = 1
  ScaleVector = (1,1,1)
  ShowElement = true
  SolverId = Placement::ExpressionEngine
  expr: Placement = LCS_Origin.Placement * AttachmentOffset * toolhead_sherpa_pcb_1515_assembly#LCS_toolhead_1515.Placement ^ -1
FEATURE [App::Part] Part002  label="XY-axis"
  Group = -> [right_motor_assembly_ab_y_motor,left_motor_assembly_ab_x_motor,linear_rail_assembly_y_rails,linear_rail_assembly_x_rail,Y_carrier_left,Y_carrier_right,xy_belt,extruder_cable_mounter,y_endstop,x_endstop_flag001,sherpa_mini,front_right_idler,front_left_idler,toolhead_sherp_pcb_1515]
  Origin = -> Origin003
FEATURE [App::Link] right_panel  label="right-panel"
  AttachedBy = #LCS_right_panel
  AttachedTo = Parent Assembly#LCS_Origin
  AttachmentOffset = pos=(188,25,25) rot=(0,0,1;1.5708rad)
  ElementCount = 0
  LinkPlacement = pos=(188,25,25) rot=(0,0,1;1.5708rad)
  LinkTransform = false
  Placement = pos=(188,25,25) rot=(0,0,1;1.5708rad)
  Scale = 1
  ScaleVector = (1,1,1)
  ShowElement = true
  SolverId = Placement::ExpressionEngine
  expr: Placement = LCS_Origin.Placement * AttachmentOffset * right_panel_assembly#LCS_right_panel.Placement ^ -1
FEATURE [App::Part] Part001  label="panel"
  Group = -> [bottom_panel_assembly,left_panel,rear_bottom_panel,rear_top_panel,front_panel,right_panel]
  Origin = -> Origin002
FEATURE [App::Link] aux_fan  label="aux-fan"
  AssemblyType = Part::Link
  AttachedBy = #LCS_aux_fan
  AttachedTo = Parent Assembly#LCS_Origin
  AttachmentOffset = pos=(-180,130,210) rot=(0,0,1;1.5708rad)
  ElementCount = 0
  LinkPlacement = pos=(-180,130,210) rot=(0,0,1;1.5708rad)
  LinkTransform = false
  Placement = pos=(-180,130,210) rot=(0,0,1;1.5708rad)
  Scale = 1
  ScaleVector = (1,1,1)
  ShowElement = true
  SolverId = Asm4EE
  expr: Placement = LCS_Origin.Placement * AttachmentOffset * Unnamed1#LCS_aux_fan.Placement ^ -1
FEATURE [App::Part] Model  label="snakeoilxy-180"
  Configuration = 0
  Group = -> [LCS_Origin,Constraints,Variables,frame_assembly_main_frame,Part,Part001,Part002,Part003,Part004,aux_fan]
  Origin = -> Origin
  Type = Assembly4 Model
